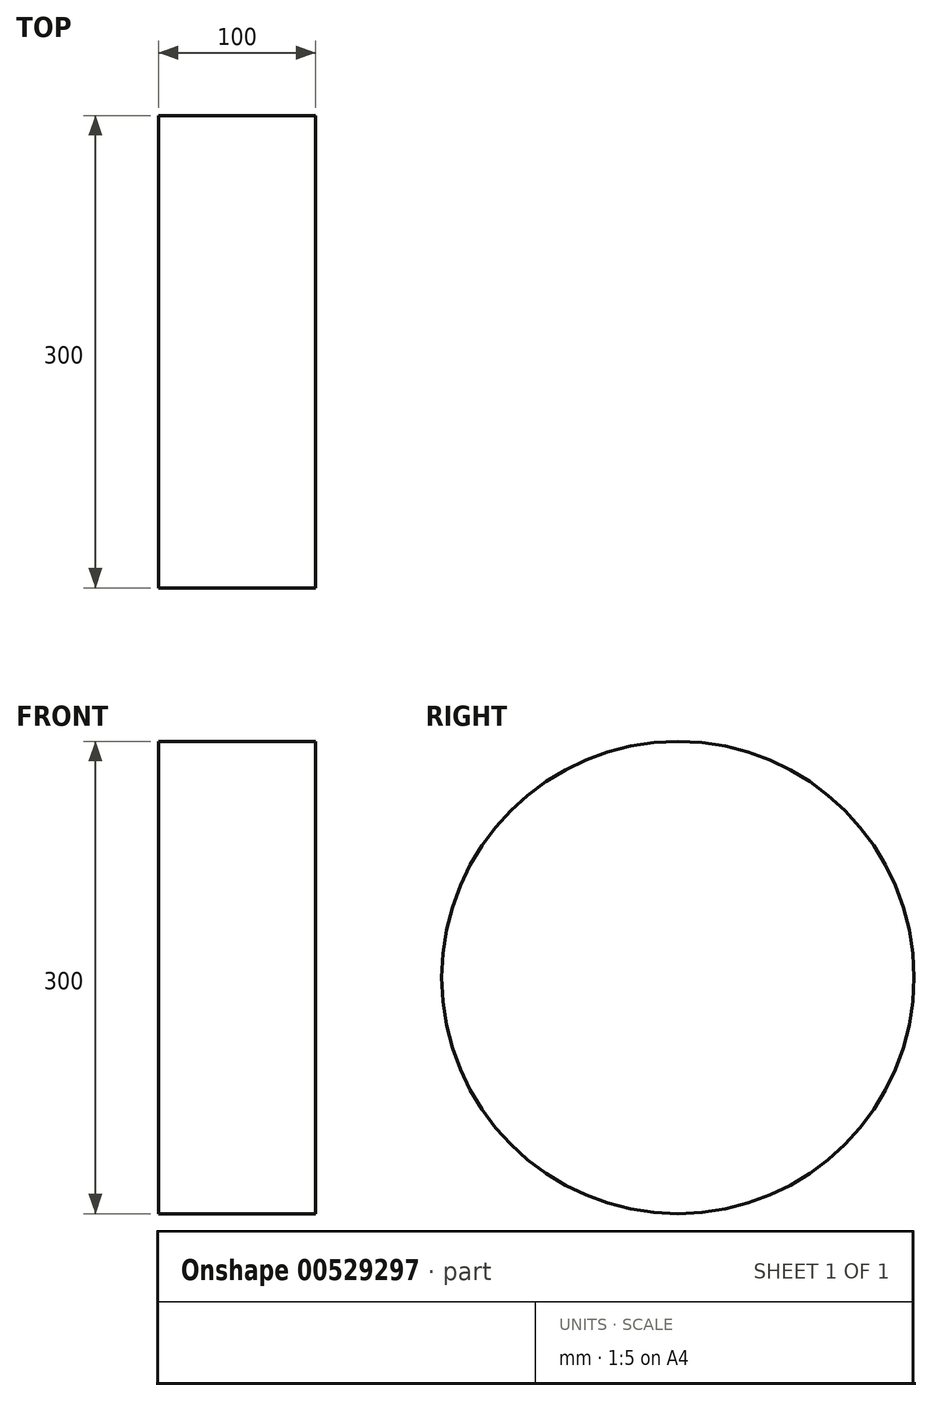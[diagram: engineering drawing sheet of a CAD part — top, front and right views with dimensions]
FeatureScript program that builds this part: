
annotation { "Feature Type Name" : "Feature", "Feature Type Description" : "" }
export const myFeature = defineFeature(function(context is Context, id is Id, definition is map)
    precondition{}
    {
        {
            var Q0;
            Q0=qCreatedBy(makeId("Right.planeOp"),FACE);
            var sketch = newSketch(context, id + "F0", { "sketchPlane" : qUnion([Q0])});
            skCircle(sketch, "E0", {"center": v(0, 0) * mm, "radius": 150 * mm});
            skSolve(sketch);
        }
        {
            var Q0;
            Q0 = qSketchRegion(id + "F0", true);
            extrude(context, id + "F1", {"entities" : qUnion([Q0]), "depth" : 100 * mm, "offsetDistance" : 25 * mm});
        }
    });
